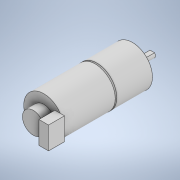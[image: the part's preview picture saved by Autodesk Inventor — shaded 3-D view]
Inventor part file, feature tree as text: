
AUTODESK INVENTOR PART (.ipt)
format: ipt  version: 2022 (Build 260153000, 153)  size: 161,280 bytes
history: native  units: mm
features: sketch x7, extrude x6, other x1, revolve x1
ambient origin geometry x8: Origin, YZ Plane, XZ Plane, XY Plane, X Axis, Y Axis, Z Axis, Center Point
bodies: Body1 (feature_tree)
feature tree (15):
  other  "Твердое тело1"
  extrude  "Выдавливание1"  Depth=25.0mm
  extrude  "Выдавливание2"  Depth=55.4mm TaperAngle=0.0deg
  extrude  "Выдавливание3"  Depth=13.5mm
  extrude  "Выдавливание4"  Depth=6.55mm TaperAngle=0.0deg
  extrude  "Выдавливание5"  Depth=6.0mm
  extrude  "Выдавливание6"  Depth=14.0mm
  revolve  "Вращение1"
  sketch  "Эскиз1"
  sketch  "Эскиз2"
  sketch  "Эскиз3"
  sketch  "Эскиз4"
  sketch  "Эскиз5"
  sketch  "Эскиз6"
  sketch  "Эскиз7"
